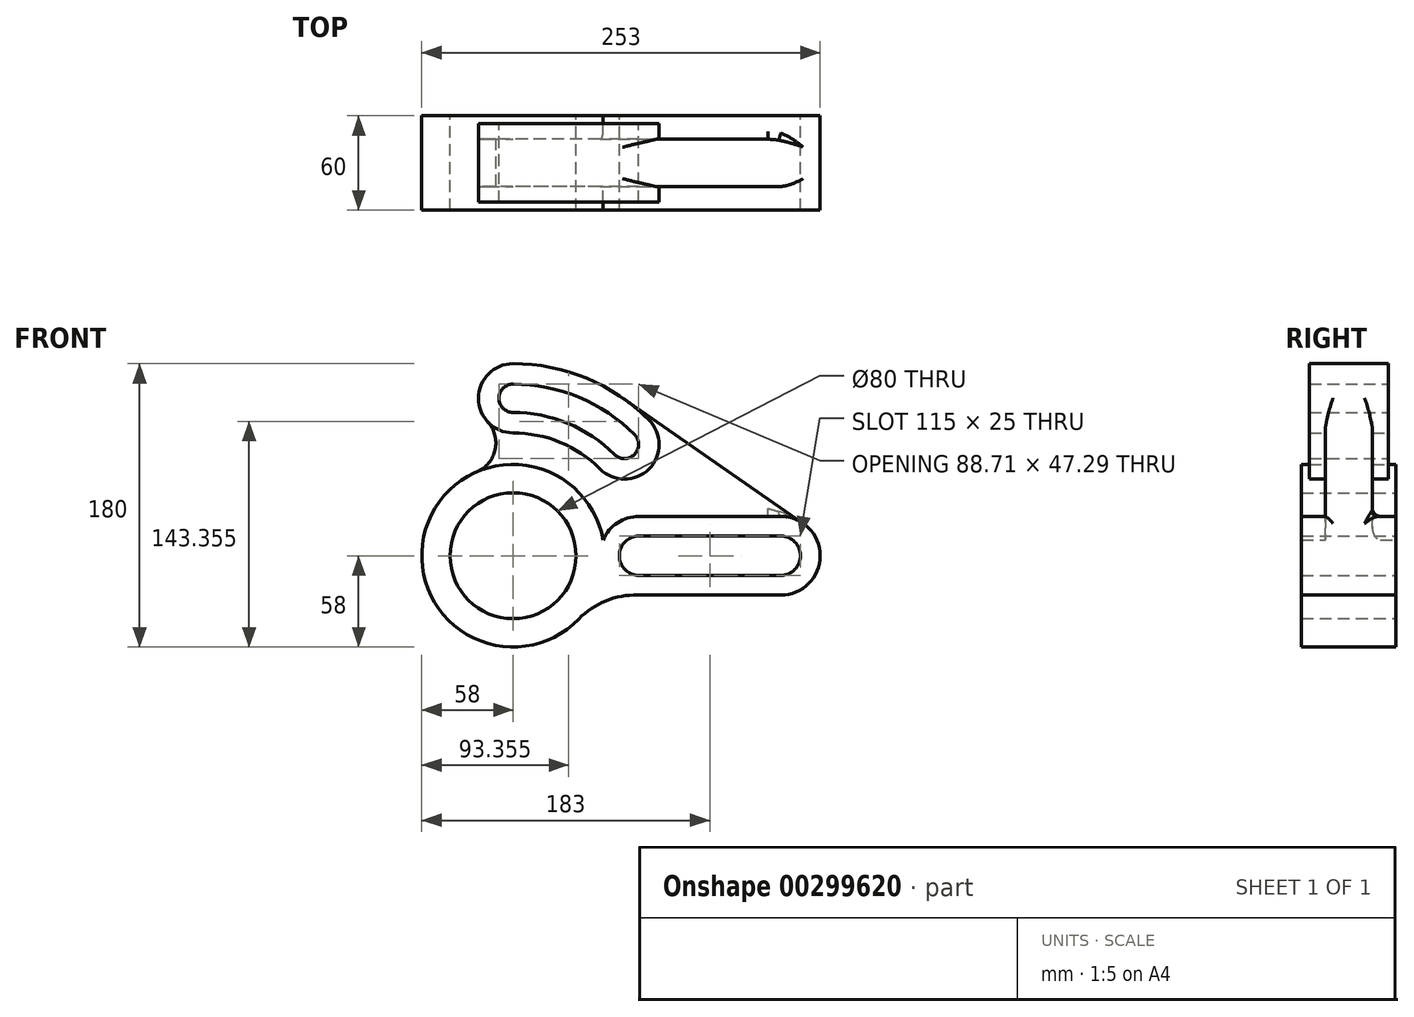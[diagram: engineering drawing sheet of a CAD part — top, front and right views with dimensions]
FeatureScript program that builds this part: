
annotation { "Feature Type Name" : "Feature", "Feature Type Description" : "" }
export const myFeature = defineFeature(function(context is Context, id is Id, definition is map)
    precondition{}
    {
        {
            var Q0;
            Q0=qCreatedBy(makeId("Front.planeOp"),FACE);
            var sketch = newSketch(context, id + "F0", { "sketchPlane" : qUnion([Q0])});
            skCircle(sketch, "E0", {"center": v(0, 0) * mm, "radius": 58 * mm});
            skCircle(sketch, "E1", {"center": v(0, 0) * mm, "radius": 40 * mm});
            skSolve(sketch);
        }
        {
            var Q0;
            Q0 = qSketchRegion(id + "F0", true);
            extrude(context, id + "F1", {"entities" : qUnion([Q0]), "endBound" : BoundingType.SYMMETRIC, "depth" : 60 * mm});
        }
        {
            var Q0;
            Q0=qCreatedBy(makeId("Front.planeOp"),FACE);
            var sketch = newSketch(context, id + "F2", { "sketchPlane" : qUnion([Q0])});
            skLineSegment(sketch, "E2", {"start": v(80, 0) * mm, "end": v(170, 0) * mm, "construction": true});
            skArc(sketch, "E3.0.startCap", {"start": v(80, -12.5) * mm, "mid": v(67.5, 0) * mm, "end": v(80, 12.5) * mm});
            skArc(sketch, "E3.0.endCap", {"start": v(170, 12.5) * mm, "mid": v(182.5, 0) * mm, "end": v(170, -12.5) * mm});
            skLineSegment(sketch, "E3.0.left", {"start": v(80, 12.5) * mm, "end": v(170, 12.5) * mm});
            skLineSegment(sketch, "E3.0.right", {"start": v(80, -12.5) * mm, "end": v(170, -12.5) * mm});
            skLineSegment(sketch, "E4.0", {"start": v(80, 25) * mm, "end": v(170, 25) * mm});
            skArc(sketch, "E4.1", {"start": v(80, -25) * mm, "mid": v(55, 0) * mm, "end": v(80, 25) * mm});
            skLineSegment(sketch, "E4.2", {"start": v(80, -25) * mm, "end": v(170, -25) * mm});
            skArc(sketch, "E4.3", {"start": v(170, 25) * mm, "mid": v(195, 0) * mm, "end": v(170, -25) * mm});
            skSolve(sketch);
        }
        {
            var Q0;
            Q0 = qSketchRegion(id + "F2", true);
            extrude(context, id + "F3", {"entities" : qUnion([Q0]), "operationType" : NewBodyOperationType.ADD, "endBound" : BoundingType.SYMMETRIC, "depth" : 60 * mm});
        }
        {
            var Q0;
            Q0=qCreatedBy(makeId("Front.planeOp"),FACE);
            var sketch = newSketch(context, id + "F4", { "sketchPlane" : qUnion([Q0])});
            skArc(sketch, "E5", {"start": v(0, 100) * mm, "mid": v(38.27, 92.39) * mm, "end": v(70.71, 70.71) * mm, "construction": true});
            skArc(sketch, "E6.0.startCap", {"start": v(0, 91) * mm, "mid": v(-9, 100) * mm, "end": v(0, 109) * mm});
            skArc(sketch, "E6.0.endCap", {"start": v(77.07, 77.07) * mm, "mid": v(77.07, 64.35) * mm, "end": v(64.35, 64.35) * mm});
            skArc(sketch, "E6.0.left", {"start": v(0, 109) * mm, "mid": v(41.71, 100.7) * mm, "end": v(77.07, 77.07) * mm});
            skArc(sketch, "E6.0.right", {"start": v(0, 91) * mm, "mid": v(34.82, 84.07) * mm, "end": v(64.35, 64.35) * mm});
            skArc(sketch, "E7.0", {"start": v(0, 78) * mm, "mid": v(-22, 100) * mm, "end": v(0, 122) * mm});
            skArc(sketch, "E7.1", {"start": v(0, 78) * mm, "mid": v(29.85, 72.06) * mm, "end": v(55.15, 55.15) * mm});
            skArc(sketch, "E7.2", {"start": v(86.27, 86.27) * mm, "mid": v(86.27, 55.15) * mm, "end": v(55.15, 55.15) * mm});
            skArc(sketch, "E7.3", {"start": v(0, 122) * mm, "mid": v(46.69, 112.71) * mm, "end": v(86.27, 86.27) * mm});
            skLineSegment(sketch, "E8", {"start": v(0, 0) * mm, "end": v(70.71, 70.71) * mm, "construction": true});
            skSolve(sketch);
        }
        {
            var Q0;
            Q0 = qSketchRegion(id + "F4", true);
            extrude(context, id + "F5", {"entities" : qUnion([Q0]), "endBound" : BoundingType.SYMMETRIC, "depth" : 50 * mm});
        }
        {
            var Q0;
            Q0=qCreatedBy(makeId("Front.planeOp"),FACE);
            var sketch = newSketch(context, id + "F6", { "sketchPlane" : qUnion([Q0])});
            skArc(sketch, "E9", {"start": v(79.25, -24.99) * mm, "mid": v(58.88, -28.66) * mm, "end": v(41.75, -40.26) * mm});
            skArc(sketch, "E10", {"start": v(41.75, -40.26) * mm, "mid": v(52.85, -23.9) * mm, "end": v(57.8, -4.76) * mm});
            skArc(sketch, "E11", {"start": v(57.12, -10.07) * mm, "mid": v(66.03, -20.73) * mm, "end": v(79.25, -24.99) * mm});
            skArc(sketch, "E12.MirrorCS", {"start": v(79.25, 24.99) * mm, "mid": v(58.88, 28.66) * mm, "end": v(41.75, 40.26) * mm});
            skArc(sketch, "E13.MirrorCS", {"start": v(41.75, 40.26) * mm, "mid": v(52.85, 23.9) * mm, "end": v(57.8, 4.76) * mm});
            skArc(sketch, "E14.MirrorCS", {"start": v(57.12, 10.07) * mm, "mid": v(66.03, 20.73) * mm, "end": v(79.25, 24.99) * mm});
            skSolve(sketch);
        }
        {
            var Q0;
            Q0=qCreatedBy(makeId("Front.planeOp"),FACE);
            var sketch = newSketch(context, id + "F7", { "sketchPlane" : qUnion([Q0])});
            skLineSegment(sketch, "E15", {"start": v(69.61, 100.2) * mm, "end": v(184.26, 20.53) * mm});
            skArc(sketch, "E16", {"start": v(-23, 53.24) * mm, "mid": v(-11.38, 67.43) * mm, "end": v(-16.2, 85.12) * mm});
            skArc(sketch, "E17", {"start": v(0, 122) * mm, "mid": v(-20.14, 108.85) * mm, "end": v(-16.2, 85.12) * mm});
            skArc(sketch, "E18", {"start": v(69.61, 100.2) * mm, "mid": v(36.47, 116.42) * mm, "end": v(0, 122) * mm});
            skArc(sketch, "E19", {"start": v(57.53, 7.4) * mm, "mid": v(28.7, 50.4) * mm, "end": v(-23, 53.24) * mm});
            skArc(sketch, "E20", {"start": v(80, 25) * mm, "mid": v(66.34, 20.94) * mm, "end": v(57.12, 10.07) * mm});
            skLineSegment(sketch, "E21", {"start": v(80, 25) * mm, "end": v(170, 25) * mm});
            skArc(sketch, "E22", {"start": v(184.26, 20.53) * mm, "mid": v(177.47, 23.86) * mm, "end": v(170, 25) * mm});
            skSolve(sketch);
        }
        {
            var Q0;
            {var subQ0=sQuery(id+"F6.wireOp",EDGE,"E9");Q0=makeQuery(id+"F6.imprint","IMPRINT",FACE,{"disambiguationData":[TD([[makeQuery(id+"F6.imprint","IMPRINT",EDGE,{"derivedFrom":subQ0}),-1.0]])]});}
            var Q1;
            {var subQ0=sQuery(id+"F6.wireOp",EDGE,"E12.MirrorCS");Q1=makeQuery(id+"F6.imprint","IMPRINT",FACE,{"disambiguationData":[TD([[makeQuery(id+"F6.imprint","IMPRINT",EDGE,{"derivedFrom":subQ0}),1.0]])]});}
            extrude(context, id + "F8", {"entities" : qUnion([Q0, Q1]), "operationType" : NewBodyOperationType.ADD, "endBound" : BoundingType.SYMMETRIC, "depth" : 60 * mm});
        }
        {
            var Q0;
            Q0=makeQuery(id+"F7.imprint","IMPRINT",FACE,{"disambiguationData":[TD([[makeQuery(id+"F7.imprint","IMPRINT",EDGE,{"derivedFrom":sQuery(id+"F7.wireOp",EDGE,"E15")}),-1.0]])]});
            extrude(context, id + "F9", {"entities" : qUnion([Q0]), "operationType" : NewBodyOperationType.ADD, "endBound" : BoundingType.SYMMETRIC, "depth" : 30 * mm});
        }
        {
            var Q0;
            Q0=makeQuery(id+"F9.boolean.opBoolean","SPLIT",FACE,{"disambiguationData":[TD([makeQuery(id+"F5.opExtrude","SWEPT_FACE",FACE,{"disambiguationData":[OSD([sQuery(id+"F4.wireOp",EDGE,"E6.0.startCap")])]})])],"derivedFrom":makeQuery(id+"F9.opExtrude","CAP_FACE",FACE,{"disambiguationData":[OSD([sQuery(id+"F7.wireOp",EDGE,"E15"),sQuery(id+"F7.wireOp",EDGE,"E16"),sQuery(id+"F7.wireOp",EDGE,"E17"),sQuery(id+"F7.wireOp",EDGE,"E18"),sQuery(id+"F7.wireOp",EDGE,"E19"),sQuery(id+"F7.wireOp",EDGE,"E20"),sQuery(id+"F7.wireOp",EDGE,"E21"),sQuery(id+"F7.wireOp",EDGE,"E22")])],"isStart":false})});
            extrude(context, id + "F10", {"entities" : qUnion([Q0]), "operationType" : NewBodyOperationType.REMOVE, "endBound" : BoundingType.THROUGH_ALL, "oppositeDirection" : true, "depth" : 25 * mm});
        }
        {
            var Q0;
            Q0=makeQuery(id+"F9.opExtrude","CAP_EDGE",EDGE,{"disambiguationData":[OSD([sQuery(id+"F7.wireOp",EDGE,"E15")])],"isStart":false});
            var Q1;
            Q1=makeQuery(id+"F9.opExtrude","CAP_EDGE",EDGE,{"disambiguationData":[OSD([sQuery(id+"F7.wireOp",EDGE,"E15")])],"isStart":true});
            var Q2;
            Q2=makeQuery(id+"F9.opExtrude","CAP_EDGE",EDGE,{"disambiguationData":[OSD([sQuery(id+"F7.wireOp",EDGE,"E21")])],"isStart":false});
            var Q3;
            Q3=makeQuery(id+"F9.opExtrude","CAP_EDGE",EDGE,{"disambiguationData":[OSD([sQuery(id+"F7.wireOp",EDGE,"E21")])],"isStart":true});
            var Q4;
            Q4=makeQuery(id+"F9.opExtrude","SWEPT_EDGE",EDGE,{"disambiguationData":[OSD([sQuery(id+"F7.wireOp",EDGE,"E16"),sQuery(id+"F7.wireOp",EDGE,"E19")])]});
            fillet(context, id + "F11", {"entities" : qUnion([Q0, Q1, Q2, Q3, Q4]), "radius" : 5 * mm, "tangentPropagation" : true, "allowEdgeOverflow" : false});
        }
    });
